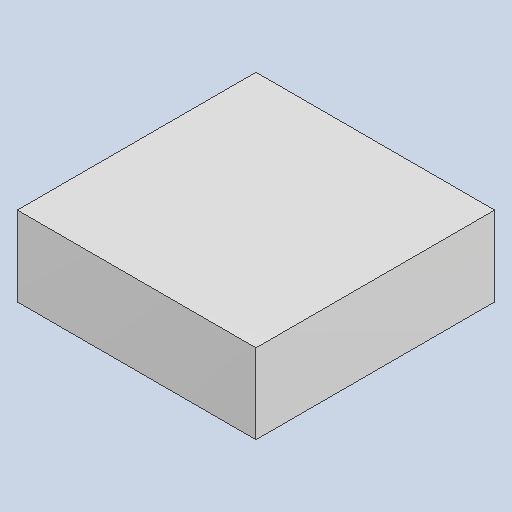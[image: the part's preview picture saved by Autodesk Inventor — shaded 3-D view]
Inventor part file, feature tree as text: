
AUTODESK INVENTOR PART (.ipt)
format: ipt  version: 2023.4 (Build 274418000, 418)  size: 79,872 bytes
history: native  units: mm
features: extrude x1
ambient origin geometry x8: Origin, YZ Plane, XZ Plane, XY Plane, X Axis, Y Axis, Z Axis, Center Point
bodies: Solid1 (feature_tree)
feature tree (1):
  extrude  "Extruded_36"  [1 undecoded]
note: 1 required parameter value undecoded (feature->parameter linkage not recoverable at this tier; creation-order binding heuristic only, values carry confidence <= 0.55)
